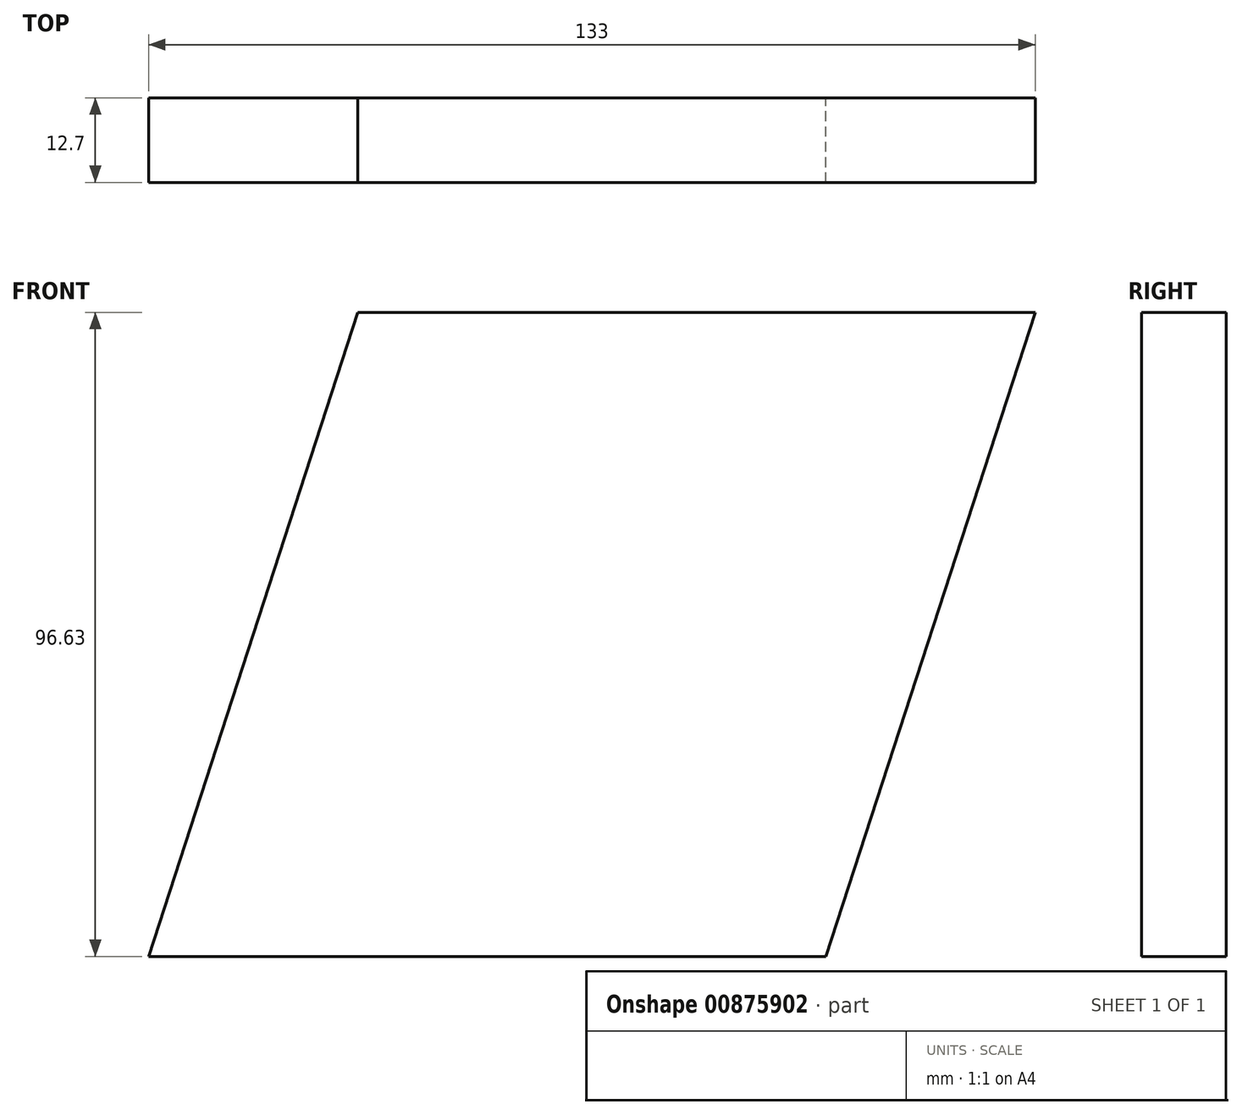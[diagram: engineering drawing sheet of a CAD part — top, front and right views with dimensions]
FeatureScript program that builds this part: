
annotation { "Feature Type Name" : "Feature", "Feature Type Description" : "" }
export const myFeature = defineFeature(function(context is Context, id is Id, definition is map)
    precondition{}
    {
        {
            var Q0;
            Q0=qCreatedBy(makeId("Front.planeOp"),FACE);
            var sketch = newSketch(context, id + "F0", { "sketchPlane" : qUnion([Q0])});
            skLineSegment(sketch, "E0", {"start": v(-269.04, 0) * mm, "end": v(-167.44, 0) * mm});
            skLineSegment(sketch, "E1", {"start": v(-167.44, 0) * mm, "end": v(-198.84, -96.63) * mm});
            skLineSegment(sketch, "E2", {"start": v(-198.84, -96.63) * mm, "end": v(-300.44, -96.63) * mm});
            skLineSegment(sketch, "E3", {"start": v(-300.44, -96.63) * mm, "end": v(-269.04, 0) * mm});
            skSolve(sketch);
        }
        {
            var Q0;
            Q0=makeQuery(id+"F0.imprint","IMPRINT",FACE,{"disambiguationData":[TD([[makeQuery(id+"F0.imprint","IMPRINT",EDGE,{"derivedFrom":sQuery(id+"F0.wireOp",EDGE,"E0")}),-1.0]])]});
            extrude(context, id + "F1", {"entities" : qUnion([Q0]), "depth" : 12.7 * mm, "offsetDistance" : 25.4 * mm});
        }
    });
